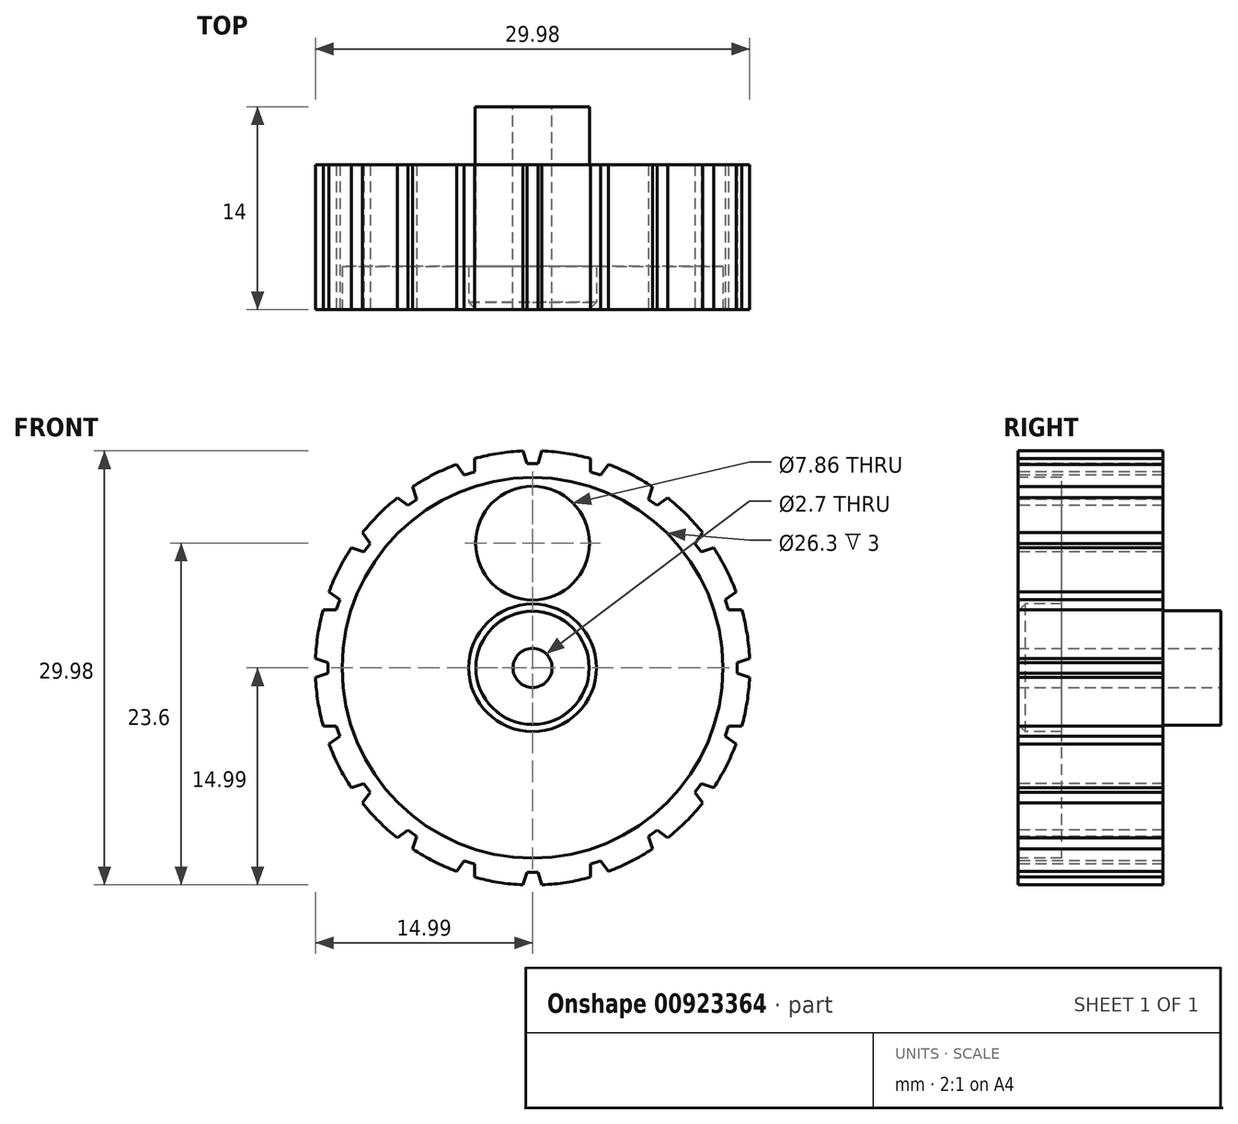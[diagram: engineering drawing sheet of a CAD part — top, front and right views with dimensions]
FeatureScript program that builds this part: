
annotation { "Feature Type Name" : "Feature", "Feature Type Description" : "" }
export const myFeature = defineFeature(function(context is Context, id is Id, definition is map)
    precondition{}
    {
        {
            var Q0;
            Q0=qCreatedBy(makeId("Front.planeOp"),FACE);
            var sketch = newSketch(context, id + "F0", { "sketchPlane" : qUnion([Q0])});
            skCircle(sketch, "E0", {"center": v(0, 0) * mm, "radius": 15 * mm});
            skCircle(sketch, "E1", {"center": v(0, 0) * mm, "radius": 1.35 * mm});
            skSolve(sketch);
        }
        {
            var Q0;
            Q0=makeQuery(id+"F0.imprint","IMPRINT",FACE,{"disambiguationData":[TD([[makeQuery(id+"F0.imprint","IMPRINT",EDGE,{"derivedFrom":sQuery(id+"F0.wireOp",EDGE,"E0")}),1.0]])]});
            extrude(context, id + "F1", {"entities" : qUnion([Q0]), "depth" : 10 * mm, "offsetDistance" : 25 * mm});
        }
        {
            var Q0;
            Q0=makeQuery(id+"F1.opExtrude","CAP_FACE",FACE,{"disambiguationData":[OSD([sQuery(id+"F0.wireOp",EDGE,"E0"),sQuery(id+"F0.wireOp",EDGE,"E1")])],"isStart":false});
            var sketch = newSketch(context, id + "F2", { "sketchPlane" : qUnion([Q0])});
            skCircle(sketch, "E2", {"center": v(0, 0) * mm, "radius": 13.15 * mm});
            skCircle(sketch, "E3", {"center": v(0, 0) * mm, "radius": 4.41 * mm});
            skSolve(sketch);
        }
        {
            var Q0;
            Q0=makeQuery(id+"F2.imprint","IMPRINT",FACE,{"disambiguationData":[TD([[makeQuery(id+"F2.imprint","IMPRINT",EDGE,{"derivedFrom":sQuery(id+"F2.wireOp",EDGE,"E2")}),1.0]])]});
            var sketch = newSketch(context, id + "F3", { "sketchPlane" : qUnion([Q0])});
            skCircle(sketch, "E4", {"center": v(0, 8.61) * mm, "radius": 3.93 * mm});
            skSolve(sketch);
        }
        {
            var Q0;
            Q0=makeQuery(id+"F3.imprint","IMPRINT",FACE,{"disambiguationData":[TD([[makeQuery(id+"F3.imprint","IMPRINT",EDGE,{"derivedFrom":sQuery(id+"F3.wireOp",EDGE,"E4")}),1.0]])]});
            var Q1;
            Q1=makeQuery(id+"FvwTpVmf4dSeCam_1.4.F3.imprint","IMPRINT",FACE,{"disambiguationData":[TD([[makeQuery(id+"FvwTpVmf4dSeCam_1.4.F3.imprint","IMPRINT",EDGE,{"derivedFrom":sQuery(id+"FvwTpVmf4dSeCam_1.4.F3.wireOp",EDGE,"E4")}),1.0]])]});
            var Q2;
            Q2=makeQuery(id+"FvwTpVmf4dSeCam_1.1.F3.imprint","IMPRINT",FACE,{"disambiguationData":[TD([[makeQuery(id+"FvwTpVmf4dSeCam_1.1.F3.imprint","IMPRINT",EDGE,{"derivedFrom":sQuery(id+"FvwTpVmf4dSeCam_1.1.F3.wireOp",EDGE,"E4")}),1.0]])]});
            var Q3;
            Q3=makeQuery(id+"FvwTpVmf4dSeCam_1.5.F3.imprint","IMPRINT",FACE,{"disambiguationData":[TD([[makeQuery(id+"FvwTpVmf4dSeCam_1.5.F3.imprint","IMPRINT",EDGE,{"derivedFrom":sQuery(id+"FvwTpVmf4dSeCam_1.5.F3.wireOp",EDGE,"E4")}),1.0]])]});
            var Q4;
            Q4=makeQuery(id+"FvwTpVmf4dSeCam_1.2.F3.imprint","IMPRINT",FACE,{"disambiguationData":[TD([[makeQuery(id+"FvwTpVmf4dSeCam_1.2.F3.imprint","IMPRINT",EDGE,{"derivedFrom":sQuery(id+"FvwTpVmf4dSeCam_1.2.F3.wireOp",EDGE,"E4")}),1.0]])]});
            var Q5;
            Q5=makeQuery(id+"FvwTpVmf4dSeCam_1.3.F3.imprint","IMPRINT",FACE,{"disambiguationData":[TD([[makeQuery(id+"FvwTpVmf4dSeCam_1.3.F3.imprint","IMPRINT",EDGE,{"derivedFrom":sQuery(id+"FvwTpVmf4dSeCam_1.3.F3.wireOp",EDGE,"E4")}),1.0]])]});
            var Q6;
            Q6=sQuery(id+"FvwTpVmf4dSeCam_1.5.F3.wireOp",EDGE,"E4");
            var Q7;
            Q7=sQuery(id+"F3.wireOp",EDGE,"E4");
            var Q8;
            Q8=sQuery(id+"FvwTpVmf4dSeCam_1.1.F3.wireOp",EDGE,"E4");
            var Q9;
            Q9=sQuery(id+"FvwTpVmf4dSeCam_1.2.F3.wireOp",EDGE,"E4");
            var Q10;
            Q10=sQuery(id+"FvwTpVmf4dSeCam_1.3.F3.wireOp",EDGE,"E4");
            var Q11;
            Q11=sQuery(id+"FvwTpVmf4dSeCam_1.4.F3.wireOp",EDGE,"E4");
            extrude(context, id + "F4", {"entities" : qUnion([Q0, Q1, Q2, Q3, Q4, Q5]), "operationType" : NewBodyOperationType.REMOVE, "surfaceEntities" : qUnion([Q6, Q7, Q8, Q9, Q10, Q11]), "oppositeDirection" : true, "depth" : 25 * mm, "offsetDistance" : 25 * mm});
        }
        {
            var Q0;
            Q0=makeQuery(id+"F2.imprint","IMPRINT",FACE,{"disambiguationData":[TD([[makeQuery(id+"F2.imprint","IMPRINT",EDGE,{"derivedFrom":sQuery(id+"F2.wireOp",EDGE,"E2")}),1.0]])]});
            extrude(context, id + "F5", {"entities" : qUnion([Q0]), "operationType" : NewBodyOperationType.REMOVE, "oppositeDirection" : true, "depth" : 3 * mm, "offsetDistance" : 25 * mm});
        }
        {
            var Q0;
            Q0=makeQuery(id+"F5.boolean.opBoolean","COPY",EDGE,{"derivedFrom":makeQuery(id+"F5.opExtrude","CAP_EDGE",EDGE,{"disambiguationData":[OSD([sQuery(id+"F2.wireOp",EDGE,"E3")])],"isStart":true})});
            chamfer(context, id + "F6", {"entities" : qUnion([Q0]), "width" : .5 * mm, "tangentPropagation" : true});
        }
        {
            var Q0;
            {var subQ0=sQuery(id+"F0.wireOp",EDGE,"E0");Q0=makeQuery(id+"F5.boolean.opBoolean","SPLIT",FACE,{"disambiguationData":[TD([makeQuery(id+"F1.opExtrude","SWEPT_FACE",FACE,{"disambiguationData":[OSD([subQ0])]})])],"derivedFrom":makeQuery(id+"F1.opExtrude","CAP_FACE",FACE,{"disambiguationData":[OSD([subQ0,sQuery(id+"F0.wireOp",EDGE,"E1")])],"isStart":false})});}
            var sketch = newSketch(context, id + "F7", { "sketchPlane" : qUnion([Q0])});
            skLineSegment(sketch, "E5", {"start": v(-0.65, 14.99) * mm, "end": v(-0.37, 14.12) * mm});
            skLineSegment(sketch, "E6", {"start": v(-0.37, 14.12) * mm, "end": v(0, 14.12) * mm});
            skLineSegment(sketch, "E7.MirrorCS", {"start": v(0.65, 14.99) * mm, "end": v(0.37, 14.12) * mm});
            skLineSegment(sketch, "E8.MirrorCS", {"start": v(0.37, 14.12) * mm, "end": v(0, 14.12) * mm});
            skSolve(sketch);
        }
        {
            var Q0;
            {var subQ1=sQuery(id+"F7.wireOp",EDGE,"E5");Q0=makeQuery(id+"F7.imprint","IMPRINT",FACE,{"disambiguationData":[TD([[makeQuery(id+"F7.imprint","IMPRINT",EDGE,{"derivedFrom":subQ1}),1.0]])]});}
            extrude(context, id + "F8", {"entities" : qUnion([Q0]), "operationType" : NewBodyOperationType.REMOVE, "oppositeDirection" : true, "depth" : 10 * mm, "offsetDistance" : 25 * mm});
        }
        {
            var Q0;
            Q0=makeQuery(id+"F8.boolean.opBoolean","COPY",FACE,{"derivedFrom":makeQuery(id+"F8.opExtrude","SWEPT_FACE",FACE,{"disambiguationData":[OSD([sQuery(id+"F7.wireOp",EDGE,"E5")])]})});
            var Q1;
            Q1=makeQuery(id+"F8.boolean.opBoolean","COPY",FACE,{"derivedFrom":makeQuery(id+"F8.opExtrude","SWEPT_FACE",FACE,{"disambiguationData":[OSD([sQuery(id+"F7.wireOp",EDGE,"E6"),sQuery(id+"F7.wireOp",EDGE,"E8.MirrorCS")])]})});
            var Q2;
            Q2=makeQuery(id+"F8.boolean.opBoolean","COPY",FACE,{"derivedFrom":makeQuery(id+"F8.opExtrude","SWEPT_FACE",FACE,{"disambiguationData":[OSD([sQuery(id+"F7.wireOp",EDGE,"E7.MirrorCS")])]})});
            var Q3;
            Q3=makeQuery(id+"F1.opExtrude","SWEPT_FACE",FACE,{"disambiguationData":[OSD([sQuery(id+"F0.wireOp",EDGE,"E0")])]});
            circularPattern(context, id + "F9", {"patternType" : PatternType.FACE, "faces" : qUnion([Q0, Q1, Q2]), "axis" : qUnion([Q3]), "angle" : 360 * degree, "instanceCount" : 20, "equalSpace" : true});
        }
        {
            var Q0;
            Q0=makeQuery(id+"F1.opExtrude","CAP_FACE",FACE,{"disambiguationData":[OSD([sQuery(id+"F0.wireOp",EDGE,"E0"),sQuery(id+"F0.wireOp",EDGE,"E1")])],"isStart":true});
            var sketch = newSketch(context, id + "F10", { "sketchPlane" : qUnion([Q0])});
            skCircle(sketch, "E9", {"center": v(0, 0) * mm, "radius": 3.95 * mm});
            skSolve(sketch);
        }
        {
            var Q0;
            Q0=makeQuery(id+"F10.imprint","IMPRINT",FACE,{"disambiguationData":[TD([[makeQuery(id+"F10.imprint","IMPRINT",EDGE,{"derivedFrom":sQuery(id+"F10.wireOp",EDGE,"E9")}),1.0]])]});
            extrude(context, id + "F11", {"entities" : qUnion([Q0]), "operationType" : NewBodyOperationType.ADD, "depth" : 4 * mm, "offsetDistance" : 25 * mm});
        }
    });
